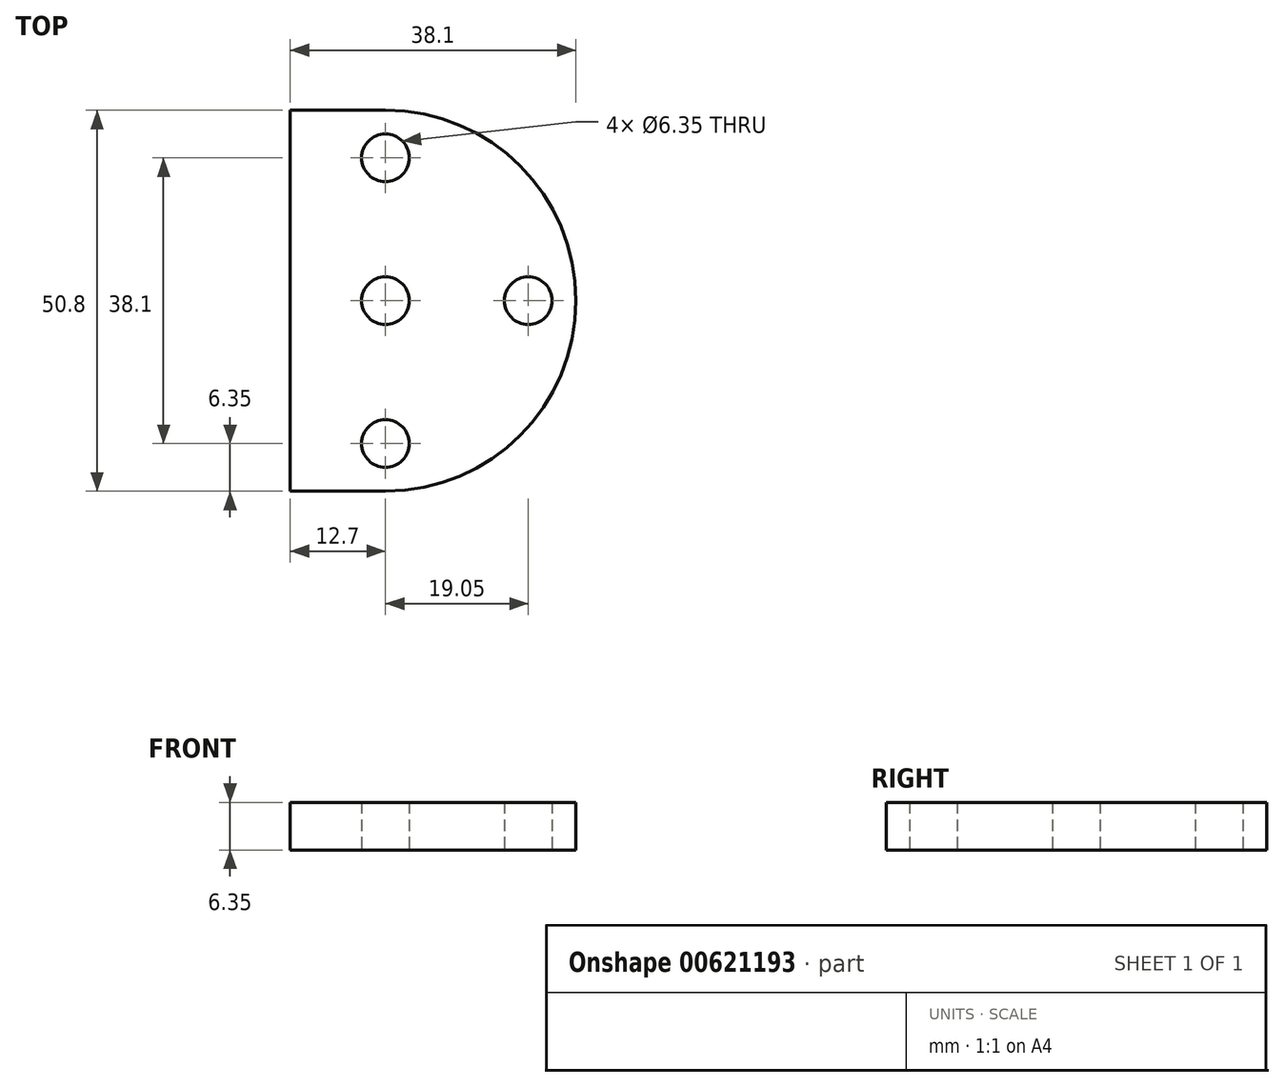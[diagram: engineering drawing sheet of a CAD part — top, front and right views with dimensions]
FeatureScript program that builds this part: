
annotation { "Feature Type Name" : "Feature", "Feature Type Description" : "" }
export const myFeature = defineFeature(function(context is Context, id is Id, definition is map)
    precondition{}
    {
        {
            var Q0;
            Q0=qCreatedBy(makeId("Top.planeOp"),FACE);
            var sketch = newSketch(context, id + "F0", { "sketchPlane" : qUnion([Q0])});
            skLineSegment(sketch, "E0.bottom", {"start": v(0, 0) * mm, "end": v(12.7, 0) * mm});
            skLineSegment(sketch, "E0.top", {"start": v(0, -50.8) * mm, "end": v(12.7, -50.8) * mm});
            skLineSegment(sketch, "E0.left", {"start": v(0, 0) * mm, "end": v(0, -50.8) * mm});
            skLineSegment(sketch, "E0.right", {"start": v(38.1, -25.4) * mm, "end": v(38.1, -25.4) * mm});
            skPoint(sketch, "E1.visualSharp", {"position": v(38.1, -50.8) * mm});
            skArc(sketch, "E1.filletArc", {"start": v(12.7, -50.8) * mm, "mid": v(30.66, -43.36) * mm, "end": v(38.1, -25.4) * mm});
            skPoint(sketch, "E2.visualSharp", {"position": v(38.1, 0) * mm});
            skArc(sketch, "E2.filletArc", {"start": v(38.1, -25.4) * mm, "mid": v(30.66, -7.44) * mm, "end": v(12.7, 0) * mm});
            skCircle(sketch, "E3", {"center": v(12.7, -25.4) * mm, "radius": 3.18 * mm});
            skLineSegment(sketch, "E4", {"start": v(12.7, -25.4) * mm, "end": v(12.7, -6.35) * mm});
            skLineSegment(sketch, "E5", {"start": v(12.7, -25.4) * mm, "end": v(31.75, -25.4) * mm});
            skLineSegment(sketch, "E6", {"start": v(12.7, -25.4) * mm, "end": v(12.7, -44.45) * mm});
            skCircle(sketch, "E7", {"center": v(12.7, -6.35) * mm, "radius": 3.18 * mm});
            skCircle(sketch, "E8", {"center": v(31.75, -25.4) * mm, "radius": 3.18 * mm});
            skCircle(sketch, "E9", {"center": v(12.7, -44.45) * mm, "radius": 3.18 * mm});
            skSolve(sketch);
        }
        {
            var Q0;
            Q0=makeQuery(id+"F0.imprint","IMPRINT",FACE,{"disambiguationData":[TD([[makeQuery(id+"F0.imprint","IMPRINT",EDGE,{"derivedFrom":sQuery(id+"F0.wireOp",EDGE,"E0.bottom")}),-1.0]])]});
            extrude(context, id + "F1", {"entities" : qUnion([Q0]), "depth" : 6.35 * mm, "offsetDistance" : 25.4 * mm});
        }
    });
